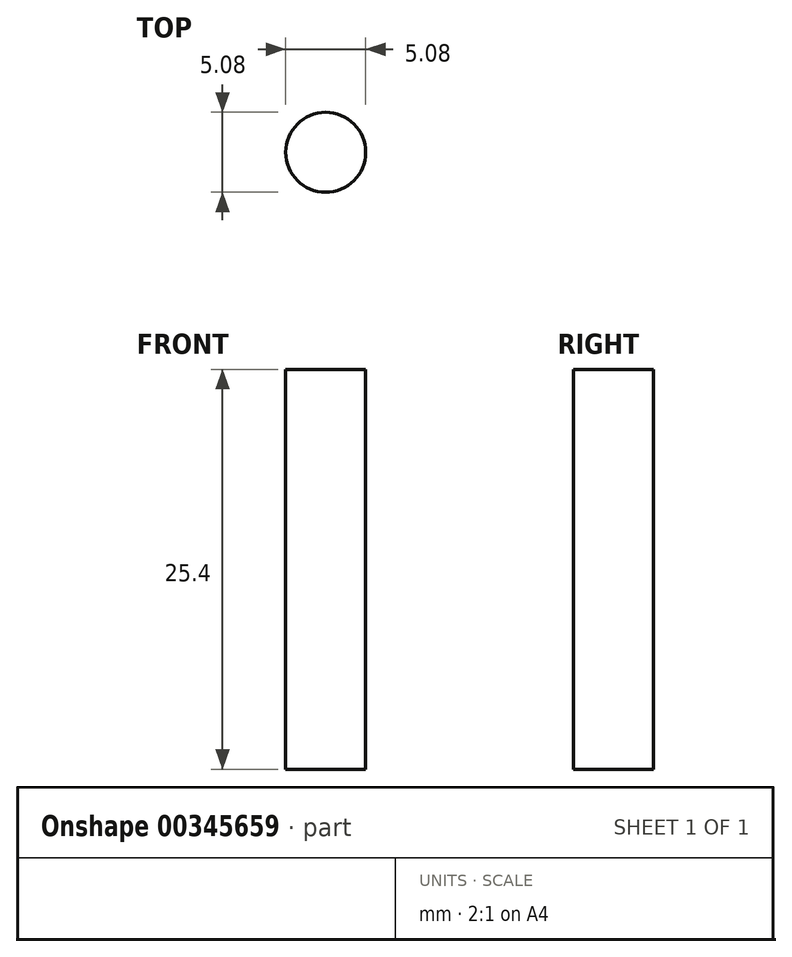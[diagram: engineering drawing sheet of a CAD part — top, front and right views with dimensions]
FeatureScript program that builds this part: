
annotation { "Feature Type Name" : "Feature", "Feature Type Description" : "" }
export const myFeature = defineFeature(function(context is Context, id is Id, definition is map)
    precondition{}
    {
        {
            var Q0;
            Q0=qCreatedBy(makeId("Top.planeOp"),FACE);
            var sketch = newSketch(context, id + "F0", { "sketchPlane" : qUnion([Q0])});
            skCircle(sketch, "E0", {"center": v(0, 0) * mm, "radius": 2.54 * mm});
            skSolve(sketch);
        }
        {
            var Q0;
            Q0=makeQuery(id+"F0.imprint","IMPRINT",FACE,{"disambiguationData":[TD([[makeQuery(id+"F0.imprint","IMPRINT",EDGE,{"derivedFrom":sQuery(id+"F0.wireOp",EDGE,"E0")}),1.0]])]});
            extrude(context, id + "F1", {"entities" : qUnion([Q0]), "depth" : 25.4 * mm});
        }
    });
